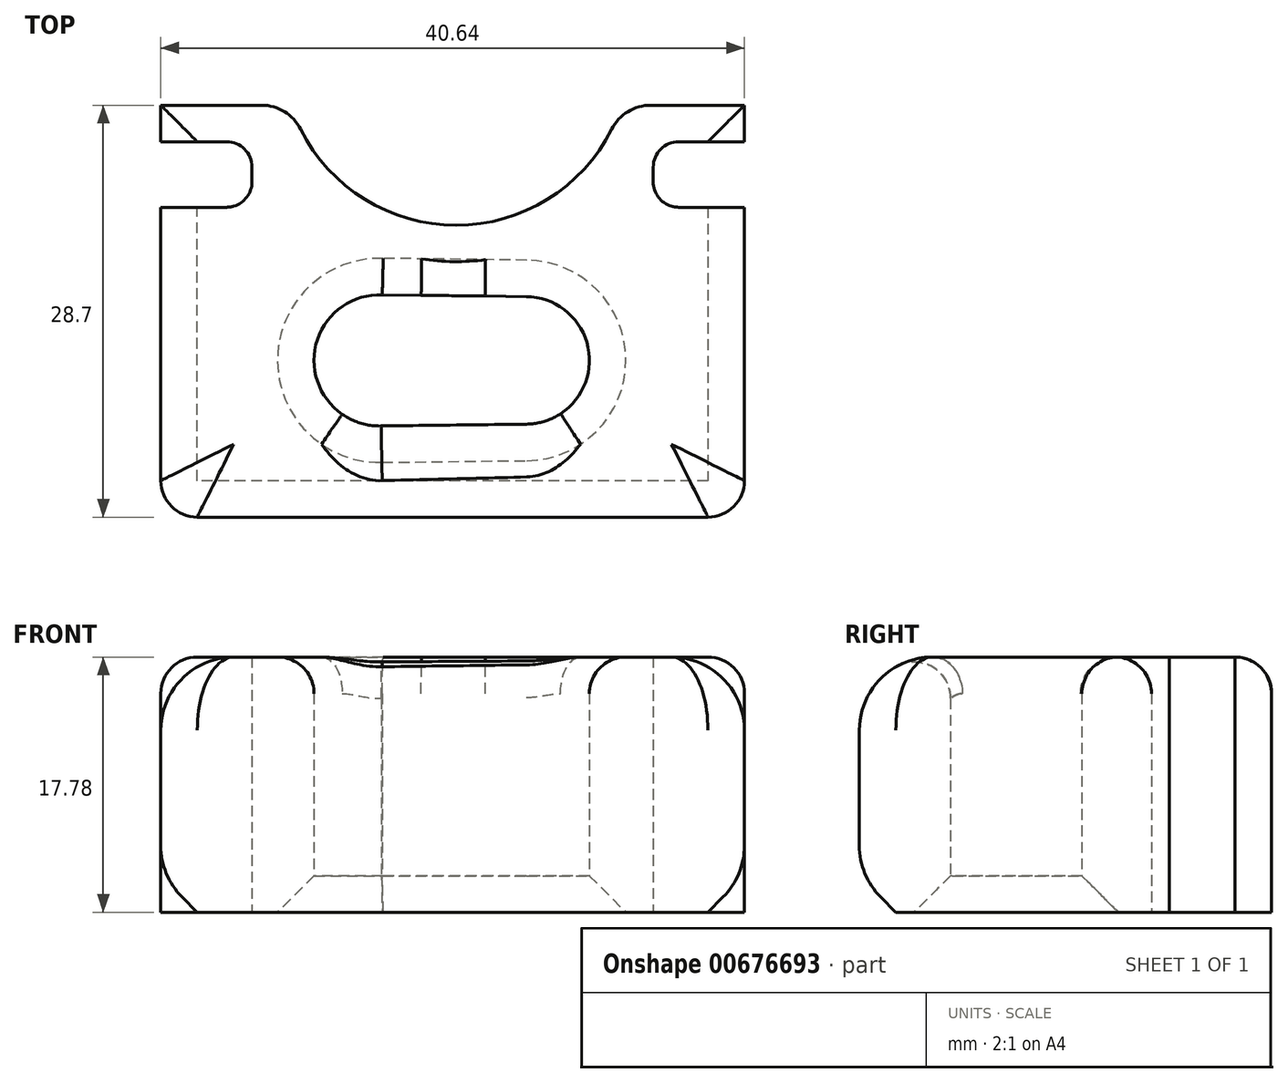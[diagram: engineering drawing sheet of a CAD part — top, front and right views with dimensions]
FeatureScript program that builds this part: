
annotation { "Feature Type Name" : "Feature", "Feature Type Description" : "" }
export const myFeature = defineFeature(function(context is Context, id is Id, definition is map)
    precondition{}
    {
        {
            var Q0;
            Q0=qCreatedBy(makeId("Top.planeOp"),FACE);
            var sketch = newSketch(context, id + "F0", { "sketchPlane" : qUnion([Q0])});
            skLineSegment(sketch, "E0.bottom", {"start": v(-25.4, 7.11) * mm, "end": v(-16.36, 7.11) * mm});
            skLineSegment(sketch, "E0.top", {"start": v(-25.4, -21.6) * mm, "end": v(15.24, -21.6) * mm});
            skLineSegment(sketch, "E0.left", {"start": v(-25.4, 7.11) * mm, "end": v(-25.4, 4.57) * mm});
            skLineSegment(sketch, "E1.bottom", {"start": v(-25.4, 4.57) * mm, "end": v(-19.05, 4.57) * mm});
            skLineSegment(sketch, "E1.top", {"start": v(-25.4, 0) * mm, "end": v(-19.05, 0) * mm});
            skLineSegment(sketch, "E1.right", {"start": v(-19.05, 4.57) * mm, "end": v(-19.05, 0) * mm});
            skLineSegment(sketch, "E2.trimOffspring", {"start": v(-25.4, 0) * mm, "end": v(-25.4, -21.6) * mm});
            skLineSegment(sketch, "E3", {"start": v(15.24, -21.6) * mm, "end": v(15.24, 0) * mm});
            skLineSegment(sketch, "E4", {"start": v(15.24, 0) * mm, "end": v(8.9, 0) * mm});
            skLineSegment(sketch, "E5", {"start": v(8.9, 0) * mm, "end": v(8.9, 4.57) * mm});
            skLineSegment(sketch, "E6", {"start": v(8.9, 4.57) * mm, "end": v(15.24, 4.57) * mm});
            skLineSegment(sketch, "E7", {"start": v(15.24, 4.57) * mm, "end": v(15.24, 7.11) * mm});
            skArc(sketch, "E8", {"start": v(-16.36, 7.11) * mm, "mid": v(-4.83, -1.25) * mm, "end": v(6.7, 7.11) * mm});
            skLineSegment(sketch, "E9.trimOffspring", {"start": v(6.7, 7.11) * mm, "end": v(15.24, 7.11) * mm});
            skLineSegment(sketch, "E10", {"start": v(-29.97, -10.67) * mm, "end": v(33.6, -10.67) * mm, "construction": true});
            skArc(sketch, "E11", {"start": v(-9.98, -6.1) * mm, "mid": v(-14.73, -10.64) * mm, "end": v(-10.03, -15.24) * mm});
            skArc(sketch, "E12", {"start": v(0.06, -15.11) * mm, "mid": v(4.44, -10.67) * mm, "end": v(0.05, -6.22) * mm});
            skLineSegment(sketch, "E13", {"start": v(-10.23, -6.1) * mm, "end": v(0.05, -6.22) * mm});
            skLineSegment(sketch, "E14", {"start": v(-10.03, -15.24) * mm, "end": v(0.06, -15.11) * mm});
            skSolve(sketch);
        }
        {
            var Q0;
            Q0=makeQuery(id+"F0.imprint","IMPRINT",FACE,{"disambiguationData":[TD([[makeQuery(id+"F0.imprint","IMPRINT",EDGE,{"derivedFrom":sQuery(id+"F0.wireOp",EDGE,"E0.bottom")}),-1.0]])]});
            extrude(context, id + "F1", {"entities" : qUnion([Q0]), "depth" : 17.78 * mm, "offsetDistance" : 25.4 * mm});
        }
        {
            var Q0;
            Q0=makeQuery(id+"F1.opExtrude","CAP_EDGE",EDGE,{"disambiguationData":[OSD([sQuery(id+"F0.wireOp",EDGE,"E8")])],"isStart":false});
            var Q1;
            Q1=makeQuery(id+"F1.opExtrude","CAP_EDGE",EDGE,{"disambiguationData":[OSD([sQuery(id+"F0.wireOp",EDGE,"E0.left")])],"isStart":false});
            var Q2;
            Q2=makeQuery(id+"F1.opExtrude","CAP_EDGE",EDGE,{"disambiguationData":[OSD([sQuery(id+"F0.wireOp",EDGE,"E7")])],"isStart":false});
            var Q3;
            Q3=makeQuery(id+"F1.opExtrude","CAP_EDGE",EDGE,{"disambiguationData":[OSD([sQuery(id+"F0.wireOp",EDGE,"E9.trimOffspring")])],"isStart":false});
            var Q4;
            Q4=makeQuery(id+"F1.opExtrude","CAP_EDGE",EDGE,{"disambiguationData":[OSD([sQuery(id+"F0.wireOp",EDGE,"E0.bottom")])],"isStart":false});
            var Q5;
            Q5=makeQuery(id+"F1.opExtrude","SWEPT_EDGE",EDGE,{"disambiguationData":[OSD([sQuery(id+"F0.wireOp",EDGE,"E0.top"),sQuery(id+"F0.wireOp",EDGE,"E2.trimOffspring")])]});
            var Q6;
            Q6=makeQuery(id+"F1.opExtrude","SWEPT_EDGE",EDGE,{"disambiguationData":[OSD([sQuery(id+"F0.wireOp",EDGE,"E0.top"),sQuery(id+"F0.wireOp",EDGE,"E3")])]});
            fillet(context, id + "F2", {"entities" : qUnion([Q0, Q1, Q2, Q3, Q4, Q5, Q6]), "radius" : 2.54 * mm, "tangentPropagation" : true, "allowEdgeOverflow" : false});
        }
        {
            var Q0;
            Q0=makeQuery(id+"F1.opExtrude","CAP_EDGE",EDGE,{"disambiguationData":[OSD([sQuery(id+"F0.wireOp",EDGE,"E0.top")])],"isStart":false});
            fillet(context, id + "F3", {"entities" : qUnion([Q0]), "radius" : 5.08 * mm, "tangentPropagation" : true, "allowEdgeOverflow" : false});
        }
        {
            var Q0;
            Q0=makeQuery(id+"F1.opExtrude","CAP_EDGE",EDGE,{"disambiguationData":[OSD([sQuery(id+"F0.wireOp",EDGE,"E0.top")])],"isStart":true});
            var Q1;
            {var subQ0=sQuery(id+"F0.wireOp",EDGE,"E2.trimOffspring");var subQ1=sQuery(id+"F0.wireOp",EDGE,"E0.top");Q1=makeQuery(id+"F2.opFillet","BLEND_EDGE",EDGE,{"blendedFrom":[makeQuery(id+"F1.opExtrude","SWEPT_EDGE",EDGE,{"disambiguationData":[OSD([subQ1,subQ0])]}),makeQuery(id+"F1.opExtrude","CAP_FACE",FACE,{"disambiguationData":[OSD([sQuery(id+"F0.wireOp",EDGE,"E0.bottom"),subQ1,sQuery(id+"F0.wireOp",EDGE,"E0.left"),sQuery(id+"F0.wireOp",EDGE,"E1.bottom"),sQuery(id+"F0.wireOp",EDGE,"E1.top"),sQuery(id+"F0.wireOp",EDGE,"E1.right"),subQ0,sQuery(id+"F0.wireOp",EDGE,"E3"),sQuery(id+"F0.wireOp",EDGE,"E4"),sQuery(id+"F0.wireOp",EDGE,"E5"),sQuery(id+"F0.wireOp",EDGE,"E6"),sQuery(id+"F0.wireOp",EDGE,"E7"),sQuery(id+"F0.wireOp",EDGE,"E8"),sQuery(id+"F0.wireOp",EDGE,"E9.trimOffspring")])],"isStart":true})],"blendedInto":[makeQuery(id+"F1.opExtrude","CAP_FACE",FACE,{"disambiguationData":[OSD([sQuery(id+"F0.wireOp",EDGE,"E0.bottom"),subQ1,sQuery(id+"F0.wireOp",EDGE,"E0.left"),sQuery(id+"F0.wireOp",EDGE,"E1.bottom"),sQuery(id+"F0.wireOp",EDGE,"E1.top"),sQuery(id+"F0.wireOp",EDGE,"E1.right"),subQ0,sQuery(id+"F0.wireOp",EDGE,"E3"),sQuery(id+"F0.wireOp",EDGE,"E4"),sQuery(id+"F0.wireOp",EDGE,"E5"),sQuery(id+"F0.wireOp",EDGE,"E6"),sQuery(id+"F0.wireOp",EDGE,"E7"),sQuery(id+"F0.wireOp",EDGE,"E8"),sQuery(id+"F0.wireOp",EDGE,"E9.trimOffspring")])],"isStart":true})]});}
            chamfer(context, id + "F4", {"entities" : qUnion([Q0, Q1]), "width" : 2.54 * mm, "tangentPropagation" : true});
        }
        {
            var Q0;
            {var subQ0=sQuery(id+"F0.wireOp",EDGE,"E0.top");Q0=makeQuery(id+"F4.opChamfer","BLEND_EDGE",EDGE,{"blendedFrom":[makeQuery(id+"F1.opExtrude","CAP_EDGE",EDGE,{"disambiguationData":[OSD([subQ0])],"isStart":true}),makeQuery(id+"F1.opExtrude","SWEPT_FACE",FACE,{"disambiguationData":[OSD([subQ0])]})],"blendedInto":[makeQuery(id+"F1.opExtrude","SWEPT_FACE",FACE,{"disambiguationData":[OSD([subQ0])]})]});}
            fillet(context, id + "F5", {"entities" : qUnion([Q0]), "radius" : 5.08 * mm, "tangentPropagation" : true, "allowEdgeOverflow" : false});
        }
        {
            var Q0;
            Q0=makeQuery(id+"F1.opExtrude","SWEPT_EDGE",EDGE,{"disambiguationData":[OSD([sQuery(id+"F0.wireOp",EDGE,"E4"),sQuery(id+"F0.wireOp",EDGE,"E5")])]});
            var Q1;
            Q1=makeQuery(id+"F1.opExtrude","SWEPT_EDGE",EDGE,{"disambiguationData":[OSD([sQuery(id+"F0.wireOp",EDGE,"E5"),sQuery(id+"F0.wireOp",EDGE,"E6")])]});
            var Q2;
            Q2=makeQuery(id+"F1.opExtrude","SWEPT_EDGE",EDGE,{"disambiguationData":[OSD([sQuery(id+"F0.wireOp",EDGE,"E1.top"),sQuery(id+"F0.wireOp",EDGE,"E1.right")])]});
            var Q3;
            Q3=makeQuery(id+"F1.opExtrude","SWEPT_EDGE",EDGE,{"disambiguationData":[OSD([sQuery(id+"F0.wireOp",EDGE,"E1.bottom"),sQuery(id+"F0.wireOp",EDGE,"E1.right")])]});
            fillet(context, id + "F6", {"entities" : qUnion([Q0, Q1, Q2, Q3]), "radius" : 1.78 * mm, "tangentPropagation" : true, "allowEdgeOverflow" : false});
        }
        {
            var Q0;
            Q0=makeQuery(id+"F1.opExtrude","SWEPT_EDGE",EDGE,{"disambiguationData":[OSD([sQuery(id+"F0.wireOp",EDGE,"E0.bottom"),sQuery(id+"F0.wireOp",EDGE,"E8")])]});
            var Q1;
            Q1=makeQuery(id+"F1.opExtrude","SWEPT_EDGE",EDGE,{"disambiguationData":[OSD([sQuery(id+"F0.wireOp",EDGE,"E8"),sQuery(id+"F0.wireOp",EDGE,"E9.trimOffspring")])]});
            var Q2;
            Q2=makeQuery(id+"F2.opFillet","BLEND_EDGE",EDGE,{"blendedFrom":[makeQuery(id+"F1.opExtrude","CAP_EDGE",EDGE,{"disambiguationData":[OSD([sQuery(id+"F0.wireOp",EDGE,"E8")])],"isStart":false}),makeQuery(id+"F1.opExtrude","CAP_EDGE",EDGE,{"disambiguationData":[OSD([sQuery(id+"F0.wireOp",EDGE,"E9.trimOffspring")])],"isStart":false})],"blendedInto":[]});
            var Q3;
            Q3=makeQuery(id+"F2.opFillet","BLEND_EDGE",EDGE,{"blendedFrom":[makeQuery(id+"F1.opExtrude","CAP_EDGE",EDGE,{"disambiguationData":[OSD([sQuery(id+"F0.wireOp",EDGE,"E0.bottom")])],"isStart":false}),makeQuery(id+"F1.opExtrude","CAP_EDGE",EDGE,{"disambiguationData":[OSD([sQuery(id+"F0.wireOp",EDGE,"E8")])],"isStart":false})],"blendedInto":[]});
            fillet(context, id + "F7", {"entities" : qUnion([Q0, Q1, Q2, Q3]), "radius" : 3.05 * mm, "tangentPropagation" : true, "allowEdgeOverflow" : false});
        }
        {
            var Q0;
            Q0=makeQuery(id+"F1.opExtrude","CAP_EDGE",EDGE,{"disambiguationData":[OSD([sQuery(id+"F0.wireOp",EDGE,"E11")])],"isStart":false});
            var Q1;
            Q1=makeQuery(id+"F1.opExtrude","CAP_EDGE",EDGE,{"disambiguationData":[OSD([sQuery(id+"F0.wireOp",EDGE,"E14")])],"isStart":false});
            var Q2;
            Q2=makeQuery(id+"F1.opExtrude","CAP_EDGE",EDGE,{"disambiguationData":[OSD([sQuery(id+"F0.wireOp",EDGE,"E13")])],"isStart":false});
            var Q3;
            Q3=makeQuery(id+"F1.opExtrude","CAP_EDGE",EDGE,{"disambiguationData":[OSD([sQuery(id+"F0.wireOp",EDGE,"E12")])],"isStart":false});
            fillet(context, id + "F8", {"entities" : qUnion([Q0, Q1, Q2, Q3]), "radius" : 2.54 * mm, "tangentPropagation" : true, "allowEdgeOverflow" : false});
        }
        {
            var Q0;
            Q0=makeQuery(id+"F1.opExtrude","CAP_EDGE",EDGE,{"disambiguationData":[OSD([sQuery(id+"F0.wireOp",EDGE,"E13")])],"isStart":true});
            var Q1;
            Q1=makeQuery(id+"F1.opExtrude","CAP_EDGE",EDGE,{"disambiguationData":[OSD([sQuery(id+"F0.wireOp",EDGE,"E14")])],"isStart":true});
            var Q2;
            Q2=makeQuery(id+"F1.opExtrude","CAP_EDGE",EDGE,{"disambiguationData":[OSD([sQuery(id+"F0.wireOp",EDGE,"E12")])],"isStart":true});
            var Q3;
            Q3=makeQuery(id+"F1.opExtrude","CAP_EDGE",EDGE,{"disambiguationData":[OSD([sQuery(id+"F0.wireOp",EDGE,"E11")])],"isStart":true});
            chamfer(context, id + "F9", {"entities" : qUnion([Q0, Q1, Q2, Q3]), "width" : 2.54 * mm, "tangentPropagation" : true});
        }
    });
